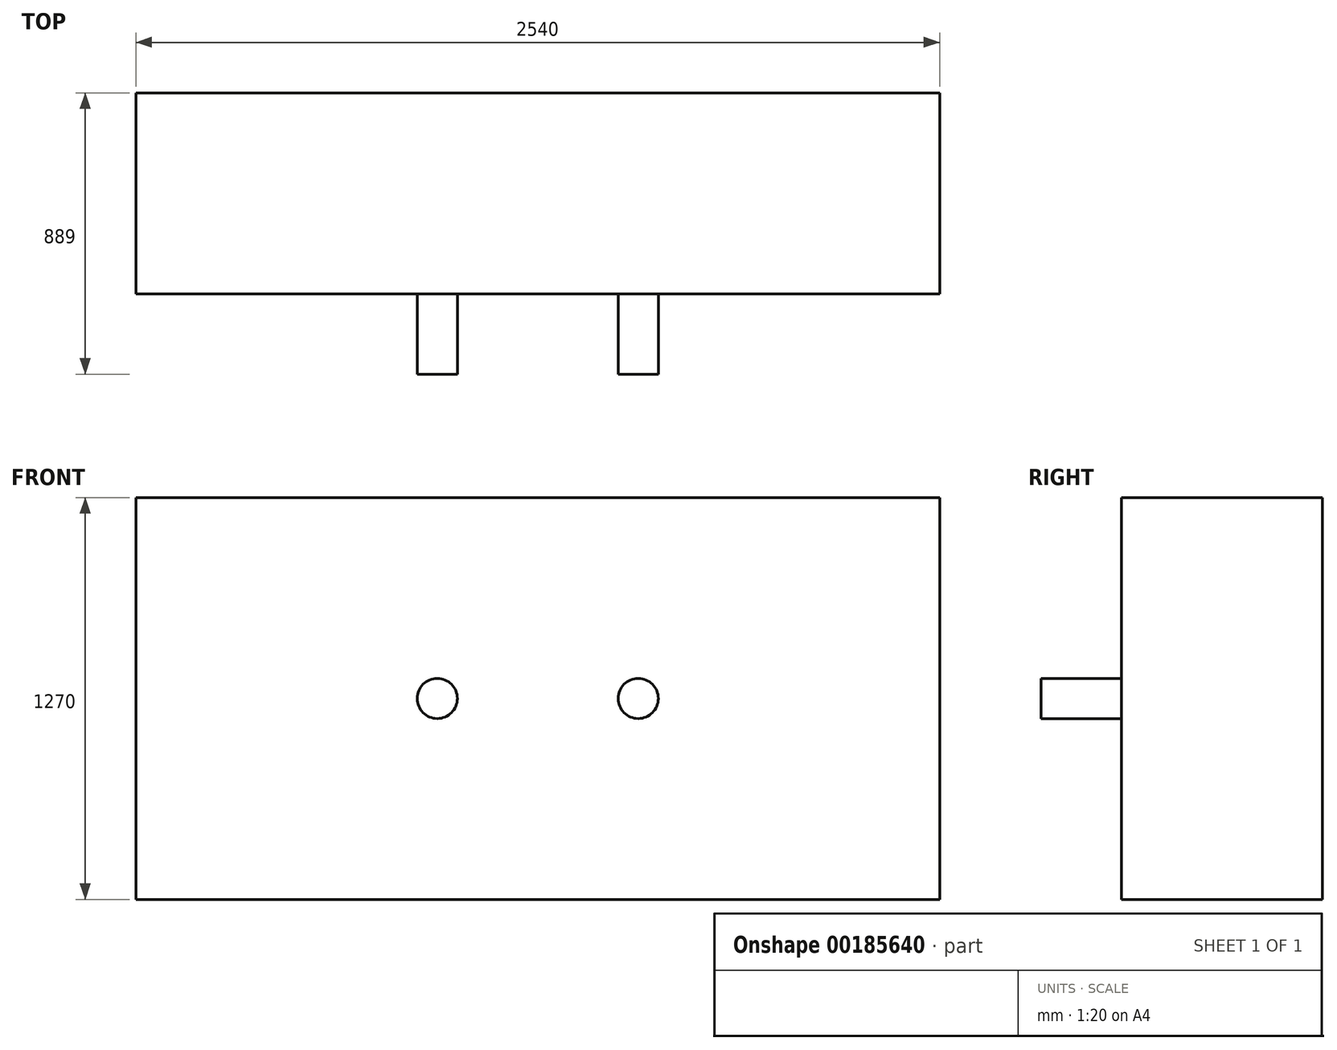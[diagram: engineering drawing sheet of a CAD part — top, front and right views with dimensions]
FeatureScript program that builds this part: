
annotation { "Feature Type Name" : "Feature", "Feature Type Description" : "" }
export const myFeature = defineFeature(function(context is Context, id is Id, definition is map)
    precondition{}
    {
        {
            var Q0;
            Q0=qCreatedBy(makeId("Front.planeOp"),FACE);
            var sketch = newSketch(context, id + "F0", { "sketchPlane" : qUnion([Q0])});
            skLineSegment(sketch, "E0.bottom", {"start": v(1270, 635) * mm, "end": v(-1270, 635) * mm});
            skLineSegment(sketch, "E0.top", {"start": v(1270, -635) * mm, "end": v(-1270, -635) * mm});
            skLineSegment(sketch, "E0.left", {"start": v(1270, 635) * mm, "end": v(1270, -635) * mm});
            skLineSegment(sketch, "E0.right", {"start": v(-1270, 635) * mm, "end": v(-1270, -635) * mm});
            skPoint(sketch, "E0.middle", {"position": v(0, 0) * mm});
            skSolve(sketch);
        }
        {
            var Q0;
            Q0 = qSketchRegion(id + "F0", true);
            extrude(context, id + "F1", {"entities" : qUnion([Q0]), "endBound" : BoundingType.SYMMETRIC, "depth" : 635 * mm});
        }
        {
            var Q0;
            Q0=makeQuery(id+"F1.opExtrude","CAP_FACE",FACE,{"disambiguationData":[OSD([sQuery(id+"F0.wireOp",EDGE,"E0.bottom"),sQuery(id+"F0.wireOp",EDGE,"E0.top"),sQuery(id+"F0.wireOp",EDGE,"E0.left"),sQuery(id+"F0.wireOp",EDGE,"E0.right")])],"isStart":false});
            var sketch = newSketch(context, id + "F2", { "sketchPlane" : qUnion([Q0])});
            skCircle(sketch, "E1", {"center": v(-317.5, 0) * mm, "radius": 63.5 * mm});
            skCircle(sketch, "E2", {"center": v(317.5, 0) * mm, "radius": 63.5 * mm});
            skLineSegment(sketch, "E3", {"start": v(0, 0) * mm, "end": v(0, 175.95) * mm, "construction": true});
            skSolve(sketch);
        }
        {
            var Q0;
            Q0 = qSketchRegion(id + "F2", true);
            extrude(context, id + "F3", {"entities" : qUnion([Q0]), "operationType" : NewBodyOperationType.ADD, "depth" : 254 * mm});
        }
    });
